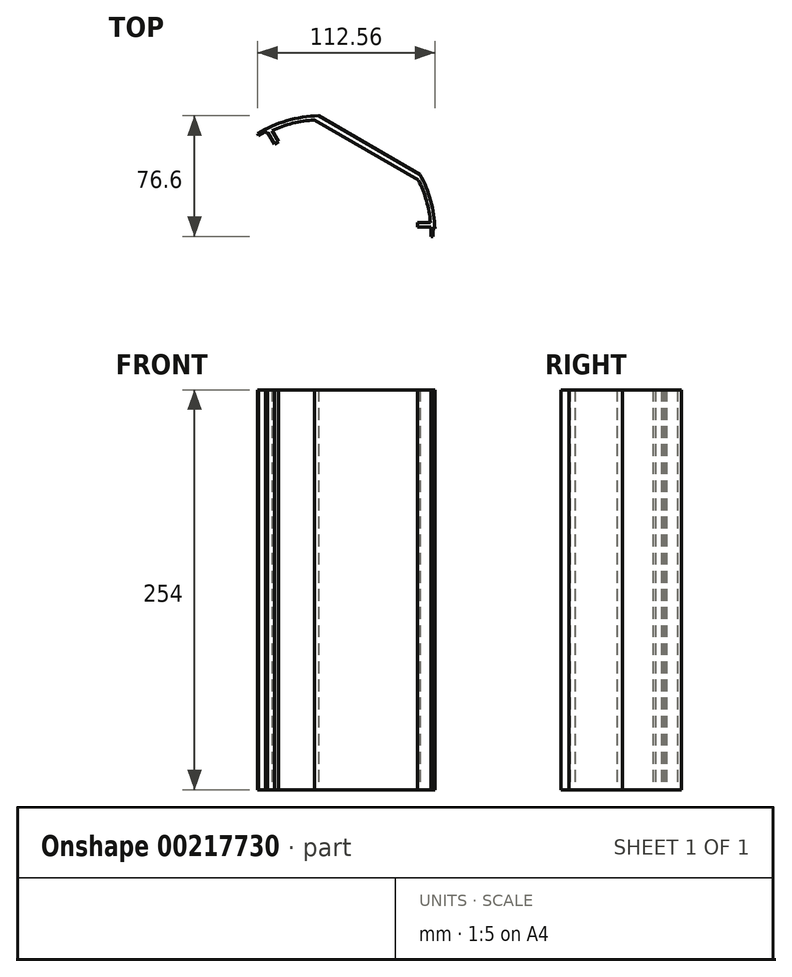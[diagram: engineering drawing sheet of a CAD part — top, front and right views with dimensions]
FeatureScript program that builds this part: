
annotation { "Feature Type Name" : "Feature", "Feature Type Description" : "" }
export const myFeature = defineFeature(function(context is Context, id is Id, definition is map)
    precondition{}
    {
        {
            var Q0;
            Q0=qCreatedBy(makeId("Top.planeOp"),FACE);
            var sketch = newSketch(context, id + "F0", { "sketchPlane" : qUnion([Q0])});
            skPoint(sketch, "E0.second.point", {"position": v(62.23, 0) * mm});
            skPoint(sketch, "E0.third.point", {"position": v(30, 27.57) * mm});
            skPoint(sketch, "E1.center", {"position": v(34.29, -0.04) * mm});
            skLineSegment(sketch, "E2", {"start": v(15.32, 43.04) * mm, "end": v(15.27, 43.25) * mm});
            skLineSegment(sketch, "E3", {"start": v(29.61, 34.8) * mm, "end": v(29.8, 34.84) * mm});
            skLineSegment(sketch, "E4", {"start": v(29.61, -34.8) * mm, "end": v(29.8, -34.83) * mm});
            skPoint(sketch, "E5.startSnap0", {"position": v(-57.75, 29.6) * mm});
            skLineSegment(sketch, "E6.0", {"start": v(-2.83, 71.35) * mm, "end": v(63.26, 33.1) * mm});
            skLineSegment(sketch, "E6.1", {"start": v(-60.27, 38.27) * mm, "end": v(-60.35, -38.12) * mm});
            skLineSegment(sketch, "E6.2", {"start": v(-2.99, -71.33) * mm, "end": v(63.25, -33.18) * mm});
            skLineSegment(sketch, "E7.0", {"start": v(-0.3, 73.99) * mm, "end": v(64.27, 36.63) * mm});
            skLineSegment(sketch, "E7.1", {"start": v(-63.82, 37.4) * mm, "end": v(-63.9, -37.24) * mm});
            skLineSegment(sketch, "E7.2", {"start": v(-0.45, -73.97) * mm, "end": v(64.27, -36.7) * mm});
            skLineSegment(sketch, "E8", {"start": v(-35.38, -61.11) * mm, "end": v(-38.56, -66.6) * mm});
            skArc(sketch, "E9", {"start": v(73.63, 2.47) * mm, "mid": v(70.96, 20.1) * mm, "end": v(64.27, 36.63) * mm});
            skArc(sketch, "E10", {"start": v(-0.3, 73.99) * mm, "mid": v(-20.38, 70.86) * mm, "end": v(-38.93, 62.54) * mm});
            skArc(sketch, "E11.0", {"start": v(-2.83, 71.35) * mm, "mid": v(-16.66, 69.25) * mm, "end": v(-29.84, 64.57) * mm});
            skArc(sketch, "E12", {"start": v(-63.9, -37.24) * mm, "mid": v(-36.89, -63.74) * mm, "end": v(-0.45, -73.97) * mm});
            skArc(sketch, "E13.0", {"start": v(-60.35, -38.12) * mm, "mid": v(-51.62, -49.04) * mm, "end": v(-40.98, -58.12) * mm});
            skArc(sketch, "E14.0", {"start": v(63.25, -33.18) * mm, "mid": v(68.33, -20.16) * mm, "end": v(70.86, -6.41) * mm});
            skLineSegment(sketch, "E15.0", {"start": v(70.63, 6.28) * mm, "end": v(62.7, 6.3) * mm});
            skLineSegment(sketch, "E16.0", {"start": v(70.62, -6.42) * mm, "end": v(62.7, -6.4) * mm});
            skLineSegment(sketch, "E17", {"start": v(70.63, 6.28) * mm, "end": v(70.86, 6.28) * mm});
            skLineSegment(sketch, "E18", {"start": v(70.62, -6.42) * mm, "end": v(70.86, -6.41) * mm});
            skLineSegment(sketch, "E19", {"start": v(62.7, 3.37) * mm, "end": v(62.7, 6.3) * mm});
            skPoint(sketch, "E20.orphan", {"position": v(71.17, -6.4) * mm});
            skLineSegment(sketch, "E21", {"start": v(62.7, -3.49) * mm, "end": v(62.7, -6.4) * mm});
            skPoint(sketch, "E22.orphan", {"position": v(62.05, -6.4) * mm});
            skLineSegment(sketch, "E23.0", {"start": v(70.63, 3.36) * mm, "end": v(62.7, 3.37) * mm});
            skLineSegment(sketch, "E24.0", {"start": v(70.62, -3.5) * mm, "end": v(62.7, -3.49) * mm});
            skLineSegment(sketch, "E25", {"start": v(70.63, 3.36) * mm, "end": v(71.05, 3.36) * mm});
            skLineSegment(sketch, "E26", {"start": v(70.62, -3.5) * mm, "end": v(71.05, -3.5) * mm});
            skArc(sketch, "E27.trimOffspring", {"start": v(70.86, 6.28) * mm, "mid": v(68.34, 20.06) * mm, "end": v(63.26, 33.1) * mm});
            skLineSegment(sketch, "E28.0", {"start": v(-29.87, -64.28) * mm, "end": v(-25.9, -57.42) * mm});
            skLineSegment(sketch, "E29.0", {"start": v(-32.4, -62.82) * mm, "end": v(-28.43, -55.95) * mm});
            skLineSegment(sketch, "E30.0", {"start": v(-40.86, -57.92) * mm, "end": v(-36.89, -51.06) * mm});
            skLineSegment(sketch, "E31.0", {"start": v(-38.33, -59.38) * mm, "end": v(-34.36, -52.52) * mm});
            skLineSegment(sketch, "E32", {"start": v(-33.82, -52.1) * mm, "end": v(-34.14, -52.65) * mm});
            skLineSegment(sketch, "E33", {"start": v(-34.36, -52.52) * mm, "end": v(-36.89, -51.06) * mm});
            skLineSegment(sketch, "E34", {"start": v(-28.33, -55.28) * mm, "end": v(-28.65, -55.83) * mm});
            skLineSegment(sketch, "E35", {"start": v(-28.43, -55.95) * mm, "end": v(-25.9, -57.42) * mm});
            skLineSegment(sketch, "E36", {"start": v(-29.87, -64.28) * mm, "end": v(-29.99, -64.48) * mm});
            skLineSegment(sketch, "E37", {"start": v(-40.86, -57.92) * mm, "end": v(-40.98, -58.12) * mm});
            skLineSegment(sketch, "E38", {"start": v(-38.33, -59.38) * mm, "end": v(-38.55, -59.75) * mm});
            skLineSegment(sketch, "E39", {"start": v(-32.4, -62.82) * mm, "end": v(-32.61, -63.19) * mm});
            skArc(sketch, "E40.trimOffspring", {"start": v(-38.55, -59.75) * mm, "mid": v(-35.62, -61.54) * mm, "end": v(-32.61, -63.19) * mm});
            skArc(sketch, "E41.trimOffspring", {"start": v(-29.99, -64.48) * mm, "mid": v(-16.81, -69.2) * mm, "end": v(-2.99, -71.33) * mm});
            skLineSegment(sketch, "E42.0", {"start": v(-40.73, 58.03) * mm, "end": v(-36.78, 51.16) * mm});
            skLineSegment(sketch, "E43.0", {"start": v(-29.73, 64.37) * mm, "end": v(-25.77, 57.5) * mm});
            skLineSegment(sketch, "E44.0", {"start": v(-38.2, 59.49) * mm, "end": v(-34.25, 52.62) * mm});
            skLineSegment(sketch, "E45.0", {"start": v(-32.26, 62.9) * mm, "end": v(-28.3, 56.04) * mm});
            skLineSegment(sketch, "E46", {"start": v(-34.25, 52.62) * mm, "end": v(-36.78, 51.16) * mm});
            skLineSegment(sketch, "E47", {"start": v(-40.73, 58.03) * mm, "end": v(-40.85, 58.23) * mm});
            skLineSegment(sketch, "E48", {"start": v(-28.3, 56.04) * mm, "end": v(-25.77, 57.5) * mm});
            skLineSegment(sketch, "E49", {"start": v(-29.73, 64.37) * mm, "end": v(-29.84, 64.57) * mm});
            skLineSegment(sketch, "E50", {"start": v(-32.26, 62.9) * mm, "end": v(-32.47, 63.28) * mm});
            skLineSegment(sketch, "E51", {"start": v(-38.2, 59.49) * mm, "end": v(-38.41, 59.86) * mm});
            skArc(sketch, "E52.trimOffspring", {"start": v(-40.85, 58.23) * mm, "mid": v(-51.51, 49.18) * mm, "end": v(-60.27, 38.27) * mm});
            skArc(sketch, "E53.trimOffspring", {"start": v(-32.47, 63.28) * mm, "mid": v(-32.87, 63.07) * mm, "end": v(-33.26, 62.87) * mm});
            skLineSegment(sketch, "E54.0", {"start": v(-38.3, 61.43) * mm, "end": v(-38.93, 62.54) * mm});
            skLineSegment(sketch, "E55.0", {"start": v(-33.26, 62.87) * mm, "end": v(-33.89, 63.96) * mm});
            skLineSegment(sketch, "E56", {"start": v(-38.3, 61.43) * mm, "end": v(-33.89, 63.96) * mm});
            skPoint(sketch, "E57.orphan", {"position": v(-36.75, 63.84) * mm});
            skPoint(sketch, "E58.orphan", {"position": v(-37.66, 60.33) * mm});
            skPoint(sketch, "E59.start.orphan", {"position": v(-35.48, 61.64) * mm});
            skLineSegment(sketch, "E60", {"start": v(71.05, -2.6) * mm, "end": v(71.05, 3.36) * mm});
            skLineSegment(sketch, "E61.0", {"start": v(71.05, -2.6) * mm, "end": v(72.34, -2.6) * mm});
            skLineSegment(sketch, "E62.0", {"start": v(71.05, 2.47) * mm, "end": v(71.05, 2.47) * mm});
            skLineSegment(sketch, "E63", {"start": v(72.34, -2.6) * mm, "end": v(72.34, 2.47) * mm});
            skLineSegment(sketch, "E64.trimOffspring", {"start": v(72.34, 2.47) * mm, "end": v(73.63, 2.47) * mm});
            skPoint(sketch, "E65.orphan", {"position": v(71.05, -0.07) * mm});
            skPoint(sketch, "E66.orphan", {"position": v(73.63, -2.6) * mm});
            skPoint(sketch, "E67.orphan", {"position": v(71.05, -2.6) * mm});
            skArc(sketch, "E68.trimOffspring", {"start": v(-35.48, 61.64) * mm, "mid": v(-36.96, 60.76) * mm, "end": v(-38.41, 59.86) * mm});
            skSolve(sketch);
        }
        {
            var Q0;
            Q0=qSketchRegion(id+"F0",true);
            extrude(context, id + "F1", {"entities" : qUnion([Q0]), "depth" : 254 * mm});
        }
    });
